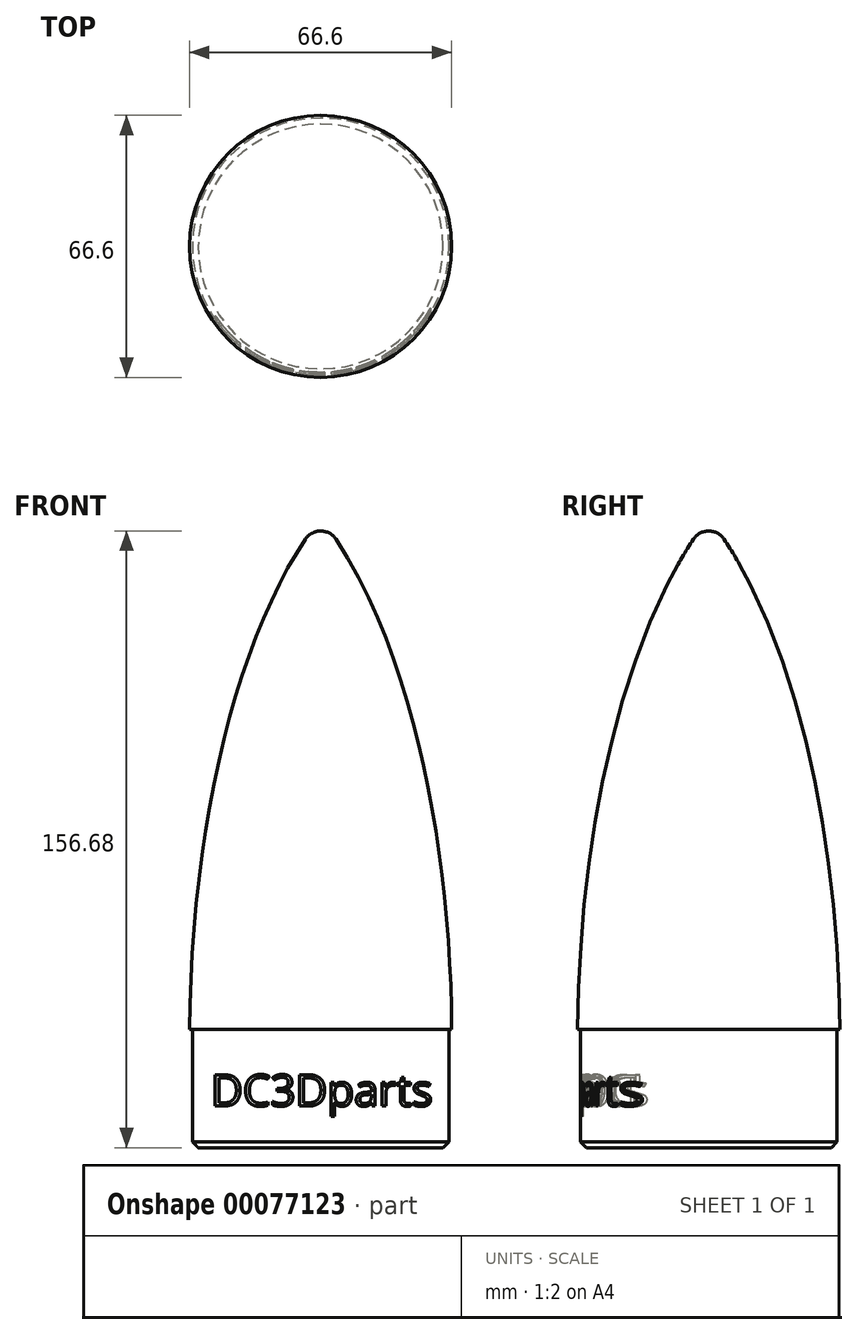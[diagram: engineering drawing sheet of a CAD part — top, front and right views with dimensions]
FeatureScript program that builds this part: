
annotation { "Feature Type Name" : "Feature", "Feature Type Description" : "" }
export const myFeature = defineFeature(function(context is Context, id is Id, definition is map)
    precondition{}
    {
        {
            var Q0;
            Q0=qCreatedBy(makeId("Front.planeOp"),FACE);
            var sketch = newSketch(context, id + "F0", { "sketchPlane" : qUnion([Q0])});
            skEllipticalArc(sketch, "E0", {});
            skLineSegment(sketch, "E1", {"start": v(-33.3, -68.75) * mm, "end": v(-32.6, -68.75) * mm});
            skLineSegment(sketch, "E2", {"start": v(0, -68.75) * mm, "end": v(0, 86.96) * mm});
            skLineSegment(sketch, "E3", {"start": v(0, -68.75) * mm, "end": v(0, -98.75) * mm});
            skLineSegment(sketch, "E4", {"start": v(0, -98.75) * mm, "end": v(-32.6, -98.75) * mm});
            skLineSegment(sketch, "E5", {"start": v(-32.6, -98.75) * mm, "end": v(-32.6, -68.75) * mm});
            skLineSegment(sketch, "E6.trimOffspring", {"start": v(-32.6, -68.75) * mm, "end": v(-33.3, -68.75) * mm});
            skArc(sketch, "E7", {"start": v(0, 57.93) * mm, "mid": v(-2.21, 57.37) * mm, "end": v(-3.9, 55.83) * mm});
            skPoint(sketch, "E8.orphan", {"position": v(0, 61.25) * mm});
            const initialGuessF0  = {"E0": [0.026576005768498712, -0.06619656694530998, 0.016311071592733244, 0.9998669656226756, 0.14465189666781272, 0.059844210815227915, 0.5734099772208412, 1.5951998253377808]};
            skSetInitialGuess(sketch, initialGuessF0);
            skSolve(sketch);
        }
        {
            var Q0;
            Q0=makeQuery(id+"F0.imprint","IMPRINT",FACE,{"disambiguationData":[TD([[makeQuery(id+"F0.imprint","IMPRINT",EDGE,{"derivedFrom":sQuery(id+"F0.wireOp",EDGE,"E0")}),1.0]])]});
            var Q1;
            Q1=sQuery(id+"F0.wireOp",EDGE,"E2");
            revolve(context, id + "F1", {"entities" : qUnion([Q0]), "axis" : qUnion([Q1]), "revolveType" : RevolveType.FULL});
        }
        {
            var Q0;
            Q0=makeQuery(id+"F1.opRevolve","SWEPT_EDGE",EDGE,{"disambiguationData":[OSD([sQuery(id+"F0.wireOp",EDGE,"E4"),sQuery(id+"F0.wireOp",EDGE,"E5")])]});
            chamfer(context, id + "F2", {"entities" : qUnion([Q0]), "width" : 1.5 * mm, "tangentPropagation" : true});
        }
        {
            var Q0;
            Q0=qCreatedBy(makeId("Front.planeOp"),FACE);
            cPlane(context, id + "F3", {"entities" : qUnion([Q0]), "cplaneType" : CPlaneType.OFFSET, "offset" : 40 * mm, "width" : 150 * mm, "height" : 150 * mm});
        }
        {
            var Q0;
            Q0=qCreatedBy(id+"F3.planeOp",FACE);
            var sketch = newSketch(context, id + "F4", { "sketchPlane" : qUnion([Q0])});
            skText(sketch, "E9", { "text": "DC3Dparts", "fontName": "OpenSans-Regular.ttf"});
            const initialGuessF4  = {"E9": [-0.02787, -0.08817, 1, 0, 0.008]};
            skSetInitialGuess(sketch, initialGuessF4);
            skSolve(sketch);
        }
        {
            var Q0;
            Q0 = qSketchRegion(id + "F4", true);
            var Q1;
            Q1=qCreatedBy(makeId("Front.planeOp"),FACE);
            extrude(context, id + "F5", {"entities" : qUnion([Q0]), "endBound" : BoundingType.UP_TO_SURFACE, "oppositeDirection" : true, "depth" : 25 * mm, "endBoundEntityFace" : qUnion([Q1]), "offsetDistance" : 25 * mm});
        }
        {
            var Q0;
            Q0=qCreatedBy(makeId("Front.planeOp"),FACE);
            var sketch = newSketch(context, id + "F6", { "sketchPlane" : qUnion([Q0])});
            skLineSegment(sketch, "E10.bottom", {"start": v(0, -71.45) * mm, "end": v(-32, -71.45) * mm});
            skLineSegment(sketch, "E10.top", {"start": v(0, -104.07) * mm, "end": v(-32, -104.07) * mm});
            skLineSegment(sketch, "E10.left", {"start": v(0, -71.45) * mm, "end": v(0, -104.07) * mm});
            skLineSegment(sketch, "E10.right", {"start": v(-32, -71.45) * mm, "end": v(-32, -104.07) * mm});
            skSolve(sketch);
        }
        {
            var Q0;
            Q0=makeQuery(id+"F6.imprint","IMPRINT",FACE,{"disambiguationData":[TD([[makeQuery(id+"F6.imprint","IMPRINT",EDGE,{"derivedFrom":sQuery(id+"F6.wireOp",EDGE,"E10.bottom")}),1.0]])]});
            var Q1;
            Q1=sQuery(id+"F6.wireOp",EDGE,"E10.left");
            revolve(context, id + "F7", {"entities" : qUnion([Q0]), "axis" : qUnion([Q1]), "revolveType" : RevolveType.FULL});
        }
        {
            var Q0;
            Q0=makeQuery(id+"F7.opRevolve","SWEPT_BODY",BODY,{"disambiguationData":[OSD([sQuery(id+"F6.wireOp",EDGE,"E10.bottom"),sQuery(id+"F6.wireOp",EDGE,"E10.top"),sQuery(id+"F6.wireOp",EDGE,"E10.left"),sQuery(id+"F6.wireOp",EDGE,"E10.right")])]});
            var Q1;
            Q1=makeQuery(id+"F5.opExtrude","SWEPT_BODY",BODY,{"disambiguationData":[OSD([sQuery(id+"F4.wireOp",EDGE,"E9.sketch_text.stroke-0"),sQuery(id+"F4.wireOp",EDGE,"E9.sketch_text.stroke-1"),sQuery(id+"F4.wireOp",EDGE,"E9.sketch_text.stroke-2"),sQuery(id+"F4.wireOp",EDGE,"E9.sketch_text.stroke-3"),sQuery(id+"F4.wireOp",EDGE,"E9.sketch_text.stroke-4"),sQuery(id+"F4.wireOp",EDGE,"E9.sketch_text.stroke-5"),sQuery(id+"F4.wireOp",EDGE,"E9.sketch_text.stroke-6"),sQuery(id+"F4.wireOp",EDGE,"E9.sketch_text.stroke-7"),sQuery(id+"F4.wireOp",EDGE,"E9.sketch_text.stroke-8"),sQuery(id+"F4.wireOp",EDGE,"E9.sketch_text.stroke-9"),sQuery(id+"F4.wireOp",EDGE,"E9.sketch_text.stroke-10"),sQuery(id+"F4.wireOp",EDGE,"E9.sketch_text.stroke-11"),sQuery(id+"F4.wireOp",EDGE,"E9.sketch_text.stroke-12"),sQuery(id+"F4.wireOp",EDGE,"E9.sketch_text.stroke-13")])]});
            var Q2;
            Q2=makeQuery(id+"F5.opExtrude","SWEPT_BODY",BODY,{"disambiguationData":[OSD([sQuery(id+"F4.wireOp",EDGE,"E9.sketch_text.stroke-14"),sQuery(id+"F4.wireOp",EDGE,"E9.sketch_text.stroke-15"),sQuery(id+"F4.wireOp",EDGE,"E9.sketch_text.stroke-16"),sQuery(id+"F4.wireOp",EDGE,"E9.sketch_text.stroke-17"),sQuery(id+"F4.wireOp",EDGE,"E9.sketch_text.stroke-18"),sQuery(id+"F4.wireOp",EDGE,"E9.sketch_text.stroke-19"),sQuery(id+"F4.wireOp",EDGE,"E9.sketch_text.stroke-20"),sQuery(id+"F4.wireOp",EDGE,"E9.sketch_text.stroke-21"),sQuery(id+"F4.wireOp",EDGE,"E9.sketch_text.stroke-22"),sQuery(id+"F4.wireOp",EDGE,"E9.sketch_text.stroke-23"),sQuery(id+"F4.wireOp",EDGE,"E9.sketch_text.stroke-24"),sQuery(id+"F4.wireOp",EDGE,"E9.sketch_text.stroke-25"),sQuery(id+"F4.wireOp",EDGE,"E9.sketch_text.stroke-26"),sQuery(id+"F4.wireOp",EDGE,"E9.sketch_text.stroke-27"),sQuery(id+"F4.wireOp",EDGE,"E9.sketch_text.stroke-28")])]});
            var Q3;
            Q3=makeQuery(id+"F5.opExtrude","SWEPT_BODY",BODY,{"disambiguationData":[OSD([sQuery(id+"F4.wireOp",EDGE,"E9.sketch_text.stroke-29"),sQuery(id+"F4.wireOp",EDGE,"E9.sketch_text.stroke-30"),sQuery(id+"F4.wireOp",EDGE,"E9.sketch_text.stroke-31"),sQuery(id+"F4.wireOp",EDGE,"E9.sketch_text.stroke-32"),sQuery(id+"F4.wireOp",EDGE,"E9.sketch_text.stroke-33"),sQuery(id+"F4.wireOp",EDGE,"E9.sketch_text.stroke-34"),sQuery(id+"F4.wireOp",EDGE,"E9.sketch_text.stroke-35"),sQuery(id+"F4.wireOp",EDGE,"E9.sketch_text.stroke-36"),sQuery(id+"F4.wireOp",EDGE,"E9.sketch_text.stroke-37"),sQuery(id+"F4.wireOp",EDGE,"E9.sketch_text.stroke-38"),sQuery(id+"F4.wireOp",EDGE,"E9.sketch_text.stroke-39"),sQuery(id+"F4.wireOp",EDGE,"E9.sketch_text.stroke-40"),sQuery(id+"F4.wireOp",EDGE,"E9.sketch_text.stroke-41"),sQuery(id+"F4.wireOp",EDGE,"E9.sketch_text.stroke-42"),sQuery(id+"F4.wireOp",EDGE,"E9.sketch_text.stroke-43"),sQuery(id+"F4.wireOp",EDGE,"E9.sketch_text.stroke-44"),sQuery(id+"F4.wireOp",EDGE,"E9.sketch_text.stroke-45"),sQuery(id+"F4.wireOp",EDGE,"E9.sketch_text.stroke-46"),sQuery(id+"F4.wireOp",EDGE,"E9.sketch_text.stroke-47"),sQuery(id+"F4.wireOp",EDGE,"E9.sketch_text.stroke-48"),sQuery(id+"F4.wireOp",EDGE,"E9.sketch_text.stroke-49"),sQuery(id+"F4.wireOp",EDGE,"E9.sketch_text.stroke-50"),sQuery(id+"F4.wireOp",EDGE,"E9.sketch_text.stroke-51"),sQuery(id+"F4.wireOp",EDGE,"E9.sketch_text.stroke-52"),sQuery(id+"F4.wireOp",EDGE,"E9.sketch_text.stroke-53"),sQuery(id+"F4.wireOp",EDGE,"E9.sketch_text.stroke-54"),sQuery(id+"F4.wireOp",EDGE,"E9.sketch_text.stroke-55"),sQuery(id+"F4.wireOp",EDGE,"E9.sketch_text.stroke-56")])]});
            var Q4;
            Q4=makeQuery(id+"F5.opExtrude","SWEPT_BODY",BODY,{"disambiguationData":[OSD([sQuery(id+"F4.wireOp",EDGE,"E9.sketch_text.stroke-57"),sQuery(id+"F4.wireOp",EDGE,"E9.sketch_text.stroke-58"),sQuery(id+"F4.wireOp",EDGE,"E9.sketch_text.stroke-59"),sQuery(id+"F4.wireOp",EDGE,"E9.sketch_text.stroke-60"),sQuery(id+"F4.wireOp",EDGE,"E9.sketch_text.stroke-61"),sQuery(id+"F4.wireOp",EDGE,"E9.sketch_text.stroke-62"),sQuery(id+"F4.wireOp",EDGE,"E9.sketch_text.stroke-63"),sQuery(id+"F4.wireOp",EDGE,"E9.sketch_text.stroke-64"),sQuery(id+"F4.wireOp",EDGE,"E9.sketch_text.stroke-65"),sQuery(id+"F4.wireOp",EDGE,"E9.sketch_text.stroke-66"),sQuery(id+"F4.wireOp",EDGE,"E9.sketch_text.stroke-67"),sQuery(id+"F4.wireOp",EDGE,"E9.sketch_text.stroke-68"),sQuery(id+"F4.wireOp",EDGE,"E9.sketch_text.stroke-69"),sQuery(id+"F4.wireOp",EDGE,"E9.sketch_text.stroke-70")])]});
            var Q5;
            Q5=makeQuery(id+"F5.opExtrude","SWEPT_BODY",BODY,{"disambiguationData":[OSD([sQuery(id+"F4.wireOp",EDGE,"E9.sketch_text.stroke-71"),sQuery(id+"F4.wireOp",EDGE,"E9.sketch_text.stroke-72"),sQuery(id+"F4.wireOp",EDGE,"E9.sketch_text.stroke-73"),sQuery(id+"F4.wireOp",EDGE,"E9.sketch_text.stroke-74"),sQuery(id+"F4.wireOp",EDGE,"E9.sketch_text.stroke-75"),sQuery(id+"F4.wireOp",EDGE,"E9.sketch_text.stroke-76"),sQuery(id+"F4.wireOp",EDGE,"E9.sketch_text.stroke-77"),sQuery(id+"F4.wireOp",EDGE,"E9.sketch_text.stroke-78"),sQuery(id+"F4.wireOp",EDGE,"E9.sketch_text.stroke-79"),sQuery(id+"F4.wireOp",EDGE,"E9.sketch_text.stroke-80"),sQuery(id+"F4.wireOp",EDGE,"E9.sketch_text.stroke-81"),sQuery(id+"F4.wireOp",EDGE,"E9.sketch_text.stroke-82"),sQuery(id+"F4.wireOp",EDGE,"E9.sketch_text.stroke-83"),sQuery(id+"F4.wireOp",EDGE,"E9.sketch_text.stroke-84"),sQuery(id+"F4.wireOp",EDGE,"E9.sketch_text.stroke-85"),sQuery(id+"F4.wireOp",EDGE,"E9.sketch_text.stroke-86"),sQuery(id+"F4.wireOp",EDGE,"E9.sketch_text.stroke-87"),sQuery(id+"F4.wireOp",EDGE,"E9.sketch_text.stroke-88"),sQuery(id+"F4.wireOp",EDGE,"E9.sketch_text.stroke-89"),sQuery(id+"F4.wireOp",EDGE,"E9.sketch_text.stroke-90"),sQuery(id+"F4.wireOp",EDGE,"E9.sketch_text.stroke-91"),sQuery(id+"F4.wireOp",EDGE,"E9.sketch_text.stroke-92"),sQuery(id+"F4.wireOp",EDGE,"E9.sketch_text.stroke-93"),sQuery(id+"F4.wireOp",EDGE,"E9.sketch_text.stroke-94"),sQuery(id+"F4.wireOp",EDGE,"E9.sketch_text.stroke-95")])]});
            var Q6;
            Q6=makeQuery(id+"F5.opExtrude","SWEPT_BODY",BODY,{"disambiguationData":[OSD([sQuery(id+"F4.wireOp",EDGE,"E9.sketch_text.stroke-136"),sQuery(id+"F4.wireOp",EDGE,"E9.sketch_text.stroke-137"),sQuery(id+"F4.wireOp",EDGE,"E9.sketch_text.stroke-138"),sQuery(id+"F4.wireOp",EDGE,"E9.sketch_text.stroke-139"),sQuery(id+"F4.wireOp",EDGE,"E9.sketch_text.stroke-140"),sQuery(id+"F4.wireOp",EDGE,"E9.sketch_text.stroke-141"),sQuery(id+"F4.wireOp",EDGE,"E9.sketch_text.stroke-142"),sQuery(id+"F4.wireOp",EDGE,"E9.sketch_text.stroke-143"),sQuery(id+"F4.wireOp",EDGE,"E9.sketch_text.stroke-144"),sQuery(id+"F4.wireOp",EDGE,"E9.sketch_text.stroke-145"),sQuery(id+"F4.wireOp",EDGE,"E9.sketch_text.stroke-146"),sQuery(id+"F4.wireOp",EDGE,"E9.sketch_text.stroke-147"),sQuery(id+"F4.wireOp",EDGE,"E9.sketch_text.stroke-148"),sQuery(id+"F4.wireOp",EDGE,"E9.sketch_text.stroke-149"),sQuery(id+"F4.wireOp",EDGE,"E9.sketch_text.stroke-150"),sQuery(id+"F4.wireOp",EDGE,"E9.sketch_text.stroke-151"),sQuery(id+"F4.wireOp",EDGE,"E9.sketch_text.stroke-152"),sQuery(id+"F4.wireOp",EDGE,"E9.sketch_text.stroke-153"),sQuery(id+"F4.wireOp",EDGE,"E9.sketch_text.stroke-154")])]});
            var Q7;
            Q7=makeQuery(id+"F5.opExtrude","SWEPT_BODY",BODY,{"disambiguationData":[OSD([sQuery(id+"F4.wireOp",EDGE,"E9.sketch_text.stroke-155"),sQuery(id+"F4.wireOp",EDGE,"E9.sketch_text.stroke-156"),sQuery(id+"F4.wireOp",EDGE,"E9.sketch_text.stroke-157"),sQuery(id+"F4.wireOp",EDGE,"E9.sketch_text.stroke-158"),sQuery(id+"F4.wireOp",EDGE,"E9.sketch_text.stroke-159"),sQuery(id+"F4.wireOp",EDGE,"E9.sketch_text.stroke-160"),sQuery(id+"F4.wireOp",EDGE,"E9.sketch_text.stroke-161"),sQuery(id+"F4.wireOp",EDGE,"E9.sketch_text.stroke-162"),sQuery(id+"F4.wireOp",EDGE,"E9.sketch_text.stroke-163"),sQuery(id+"F4.wireOp",EDGE,"E9.sketch_text.stroke-164"),sQuery(id+"F4.wireOp",EDGE,"E9.sketch_text.stroke-165"),sQuery(id+"F4.wireOp",EDGE,"E9.sketch_text.stroke-166"),sQuery(id+"F4.wireOp",EDGE,"E9.sketch_text.stroke-167"),sQuery(id+"F4.wireOp",EDGE,"E9.sketch_text.stroke-168"),sQuery(id+"F4.wireOp",EDGE,"E9.sketch_text.stroke-169"),sQuery(id+"F4.wireOp",EDGE,"E9.sketch_text.stroke-170"),sQuery(id+"F4.wireOp",EDGE,"E9.sketch_text.stroke-171"),sQuery(id+"F4.wireOp",EDGE,"E9.sketch_text.stroke-172"),sQuery(id+"F4.wireOp",EDGE,"E9.sketch_text.stroke-173"),sQuery(id+"F4.wireOp",EDGE,"E9.sketch_text.stroke-174"),sQuery(id+"F4.wireOp",EDGE,"E9.sketch_text.stroke-175"),sQuery(id+"F4.wireOp",EDGE,"E9.sketch_text.stroke-176"),sQuery(id+"F4.wireOp",EDGE,"E9.sketch_text.stroke-177"),sQuery(id+"F4.wireOp",EDGE,"E9.sketch_text.stroke-178"),sQuery(id+"F4.wireOp",EDGE,"E9.sketch_text.stroke-179")])]});
            var Q8;
            Q8=makeQuery(id+"F5.opExtrude","SWEPT_BODY",BODY,{"disambiguationData":[OSD([sQuery(id+"F4.wireOp",EDGE,"E9.sketch_text.stroke-96"),sQuery(id+"F4.wireOp",EDGE,"E9.sketch_text.stroke-97"),sQuery(id+"F4.wireOp",EDGE,"E9.sketch_text.stroke-98"),sQuery(id+"F4.wireOp",EDGE,"E9.sketch_text.stroke-99"),sQuery(id+"F4.wireOp",EDGE,"E9.sketch_text.stroke-100"),sQuery(id+"F4.wireOp",EDGE,"E9.sketch_text.stroke-101"),sQuery(id+"F4.wireOp",EDGE,"E9.sketch_text.stroke-102"),sQuery(id+"F4.wireOp",EDGE,"E9.sketch_text.stroke-103"),sQuery(id+"F4.wireOp",EDGE,"E9.sketch_text.stroke-104"),sQuery(id+"F4.wireOp",EDGE,"E9.sketch_text.stroke-105"),sQuery(id+"F4.wireOp",EDGE,"E9.sketch_text.stroke-106"),sQuery(id+"F4.wireOp",EDGE,"E9.sketch_text.stroke-107"),sQuery(id+"F4.wireOp",EDGE,"E9.sketch_text.stroke-108"),sQuery(id+"F4.wireOp",EDGE,"E9.sketch_text.stroke-109"),sQuery(id+"F4.wireOp",EDGE,"E9.sketch_text.stroke-110"),sQuery(id+"F4.wireOp",EDGE,"E9.sketch_text.stroke-111"),sQuery(id+"F4.wireOp",EDGE,"E9.sketch_text.stroke-112"),sQuery(id+"F4.wireOp",EDGE,"E9.sketch_text.stroke-113"),sQuery(id+"F4.wireOp",EDGE,"E9.sketch_text.stroke-114"),sQuery(id+"F4.wireOp",EDGE,"E9.sketch_text.stroke-115"),sQuery(id+"F4.wireOp",EDGE,"E9.sketch_text.stroke-116"),sQuery(id+"F4.wireOp",EDGE,"E9.sketch_text.stroke-117"),sQuery(id+"F4.wireOp",EDGE,"E9.sketch_text.stroke-118"),sQuery(id+"F4.wireOp",EDGE,"E9.sketch_text.stroke-119"),sQuery(id+"F4.wireOp",EDGE,"E9.sketch_text.stroke-120"),sQuery(id+"F4.wireOp",EDGE,"E9.sketch_text.stroke-121"),sQuery(id+"F4.wireOp",EDGE,"E9.sketch_text.stroke-122")])]});
            var Q9;
            Q9=makeQuery(id+"F5.opExtrude","SWEPT_BODY",BODY,{"disambiguationData":[OSD([sQuery(id+"F4.wireOp",EDGE,"E9.sketch_text.stroke-123"),sQuery(id+"F4.wireOp",EDGE,"E9.sketch_text.stroke-124"),sQuery(id+"F4.wireOp",EDGE,"E9.sketch_text.stroke-125"),sQuery(id+"F4.wireOp",EDGE,"E9.sketch_text.stroke-126"),sQuery(id+"F4.wireOp",EDGE,"E9.sketch_text.stroke-127"),sQuery(id+"F4.wireOp",EDGE,"E9.sketch_text.stroke-128"),sQuery(id+"F4.wireOp",EDGE,"E9.sketch_text.stroke-129"),sQuery(id+"F4.wireOp",EDGE,"E9.sketch_text.stroke-130"),sQuery(id+"F4.wireOp",EDGE,"E9.sketch_text.stroke-131"),sQuery(id+"F4.wireOp",EDGE,"E9.sketch_text.stroke-132"),sQuery(id+"F4.wireOp",EDGE,"E9.sketch_text.stroke-133"),sQuery(id+"F4.wireOp",EDGE,"E9.sketch_text.stroke-134"),sQuery(id+"F4.wireOp",EDGE,"E9.sketch_text.stroke-135")])]});
            booleanBodies(context, id + "F8", {"operationType" : BooleanOperationType.SUBTRACTION, "tools" : qUnion([Q0]), "targets" : qUnion([Q1, Q2, Q3, Q4, Q5, Q6, Q7, Q8, Q9])});
        }
        {
            var Q0;
            Q0=makeQuery(id+"F5.opExtrude","SWEPT_BODY",BODY,{"disambiguationData":[OSD([sQuery(id+"F4.wireOp",EDGE,"E9.sketch_text.stroke-0"),sQuery(id+"F4.wireOp",EDGE,"E9.sketch_text.stroke-1"),sQuery(id+"F4.wireOp",EDGE,"E9.sketch_text.stroke-2"),sQuery(id+"F4.wireOp",EDGE,"E9.sketch_text.stroke-3"),sQuery(id+"F4.wireOp",EDGE,"E9.sketch_text.stroke-4"),sQuery(id+"F4.wireOp",EDGE,"E9.sketch_text.stroke-5"),sQuery(id+"F4.wireOp",EDGE,"E9.sketch_text.stroke-6"),sQuery(id+"F4.wireOp",EDGE,"E9.sketch_text.stroke-7"),sQuery(id+"F4.wireOp",EDGE,"E9.sketch_text.stroke-8"),sQuery(id+"F4.wireOp",EDGE,"E9.sketch_text.stroke-9"),sQuery(id+"F4.wireOp",EDGE,"E9.sketch_text.stroke-10"),sQuery(id+"F4.wireOp",EDGE,"E9.sketch_text.stroke-11"),sQuery(id+"F4.wireOp",EDGE,"E9.sketch_text.stroke-12"),sQuery(id+"F4.wireOp",EDGE,"E9.sketch_text.stroke-13")])]});
            var Q1;
            Q1=makeQuery(id+"F5.opExtrude","SWEPT_BODY",BODY,{"disambiguationData":[OSD([sQuery(id+"F4.wireOp",EDGE,"E9.sketch_text.stroke-14"),sQuery(id+"F4.wireOp",EDGE,"E9.sketch_text.stroke-15"),sQuery(id+"F4.wireOp",EDGE,"E9.sketch_text.stroke-16"),sQuery(id+"F4.wireOp",EDGE,"E9.sketch_text.stroke-17"),sQuery(id+"F4.wireOp",EDGE,"E9.sketch_text.stroke-18"),sQuery(id+"F4.wireOp",EDGE,"E9.sketch_text.stroke-19"),sQuery(id+"F4.wireOp",EDGE,"E9.sketch_text.stroke-20"),sQuery(id+"F4.wireOp",EDGE,"E9.sketch_text.stroke-21"),sQuery(id+"F4.wireOp",EDGE,"E9.sketch_text.stroke-22"),sQuery(id+"F4.wireOp",EDGE,"E9.sketch_text.stroke-23"),sQuery(id+"F4.wireOp",EDGE,"E9.sketch_text.stroke-24"),sQuery(id+"F4.wireOp",EDGE,"E9.sketch_text.stroke-25"),sQuery(id+"F4.wireOp",EDGE,"E9.sketch_text.stroke-26"),sQuery(id+"F4.wireOp",EDGE,"E9.sketch_text.stroke-27"),sQuery(id+"F4.wireOp",EDGE,"E9.sketch_text.stroke-28")])]});
            var Q2;
            Q2=makeQuery(id+"F5.opExtrude","SWEPT_BODY",BODY,{"disambiguationData":[OSD([sQuery(id+"F4.wireOp",EDGE,"E9.sketch_text.stroke-29"),sQuery(id+"F4.wireOp",EDGE,"E9.sketch_text.stroke-30"),sQuery(id+"F4.wireOp",EDGE,"E9.sketch_text.stroke-31"),sQuery(id+"F4.wireOp",EDGE,"E9.sketch_text.stroke-32"),sQuery(id+"F4.wireOp",EDGE,"E9.sketch_text.stroke-33"),sQuery(id+"F4.wireOp",EDGE,"E9.sketch_text.stroke-34"),sQuery(id+"F4.wireOp",EDGE,"E9.sketch_text.stroke-35"),sQuery(id+"F4.wireOp",EDGE,"E9.sketch_text.stroke-36"),sQuery(id+"F4.wireOp",EDGE,"E9.sketch_text.stroke-37"),sQuery(id+"F4.wireOp",EDGE,"E9.sketch_text.stroke-38"),sQuery(id+"F4.wireOp",EDGE,"E9.sketch_text.stroke-39"),sQuery(id+"F4.wireOp",EDGE,"E9.sketch_text.stroke-40"),sQuery(id+"F4.wireOp",EDGE,"E9.sketch_text.stroke-41"),sQuery(id+"F4.wireOp",EDGE,"E9.sketch_text.stroke-42"),sQuery(id+"F4.wireOp",EDGE,"E9.sketch_text.stroke-43"),sQuery(id+"F4.wireOp",EDGE,"E9.sketch_text.stroke-44"),sQuery(id+"F4.wireOp",EDGE,"E9.sketch_text.stroke-45"),sQuery(id+"F4.wireOp",EDGE,"E9.sketch_text.stroke-46"),sQuery(id+"F4.wireOp",EDGE,"E9.sketch_text.stroke-47"),sQuery(id+"F4.wireOp",EDGE,"E9.sketch_text.stroke-48"),sQuery(id+"F4.wireOp",EDGE,"E9.sketch_text.stroke-49"),sQuery(id+"F4.wireOp",EDGE,"E9.sketch_text.stroke-50"),sQuery(id+"F4.wireOp",EDGE,"E9.sketch_text.stroke-51"),sQuery(id+"F4.wireOp",EDGE,"E9.sketch_text.stroke-52"),sQuery(id+"F4.wireOp",EDGE,"E9.sketch_text.stroke-53"),sQuery(id+"F4.wireOp",EDGE,"E9.sketch_text.stroke-54"),sQuery(id+"F4.wireOp",EDGE,"E9.sketch_text.stroke-55"),sQuery(id+"F4.wireOp",EDGE,"E9.sketch_text.stroke-56")])]});
            var Q3;
            Q3=makeQuery(id+"F5.opExtrude","SWEPT_BODY",BODY,{"disambiguationData":[OSD([sQuery(id+"F4.wireOp",EDGE,"E9.sketch_text.stroke-57"),sQuery(id+"F4.wireOp",EDGE,"E9.sketch_text.stroke-58"),sQuery(id+"F4.wireOp",EDGE,"E9.sketch_text.stroke-59"),sQuery(id+"F4.wireOp",EDGE,"E9.sketch_text.stroke-60"),sQuery(id+"F4.wireOp",EDGE,"E9.sketch_text.stroke-61"),sQuery(id+"F4.wireOp",EDGE,"E9.sketch_text.stroke-62"),sQuery(id+"F4.wireOp",EDGE,"E9.sketch_text.stroke-63"),sQuery(id+"F4.wireOp",EDGE,"E9.sketch_text.stroke-64"),sQuery(id+"F4.wireOp",EDGE,"E9.sketch_text.stroke-65"),sQuery(id+"F4.wireOp",EDGE,"E9.sketch_text.stroke-66"),sQuery(id+"F4.wireOp",EDGE,"E9.sketch_text.stroke-67"),sQuery(id+"F4.wireOp",EDGE,"E9.sketch_text.stroke-68"),sQuery(id+"F4.wireOp",EDGE,"E9.sketch_text.stroke-69"),sQuery(id+"F4.wireOp",EDGE,"E9.sketch_text.stroke-70")])]});
            var Q4;
            Q4=makeQuery(id+"F5.opExtrude","SWEPT_BODY",BODY,{"disambiguationData":[OSD([sQuery(id+"F4.wireOp",EDGE,"E9.sketch_text.stroke-71"),sQuery(id+"F4.wireOp",EDGE,"E9.sketch_text.stroke-72"),sQuery(id+"F4.wireOp",EDGE,"E9.sketch_text.stroke-73"),sQuery(id+"F4.wireOp",EDGE,"E9.sketch_text.stroke-74"),sQuery(id+"F4.wireOp",EDGE,"E9.sketch_text.stroke-75"),sQuery(id+"F4.wireOp",EDGE,"E9.sketch_text.stroke-76"),sQuery(id+"F4.wireOp",EDGE,"E9.sketch_text.stroke-77"),sQuery(id+"F4.wireOp",EDGE,"E9.sketch_text.stroke-78"),sQuery(id+"F4.wireOp",EDGE,"E9.sketch_text.stroke-79"),sQuery(id+"F4.wireOp",EDGE,"E9.sketch_text.stroke-80"),sQuery(id+"F4.wireOp",EDGE,"E9.sketch_text.stroke-81"),sQuery(id+"F4.wireOp",EDGE,"E9.sketch_text.stroke-82"),sQuery(id+"F4.wireOp",EDGE,"E9.sketch_text.stroke-83"),sQuery(id+"F4.wireOp",EDGE,"E9.sketch_text.stroke-84"),sQuery(id+"F4.wireOp",EDGE,"E9.sketch_text.stroke-85"),sQuery(id+"F4.wireOp",EDGE,"E9.sketch_text.stroke-86"),sQuery(id+"F4.wireOp",EDGE,"E9.sketch_text.stroke-87"),sQuery(id+"F4.wireOp",EDGE,"E9.sketch_text.stroke-88"),sQuery(id+"F4.wireOp",EDGE,"E9.sketch_text.stroke-89"),sQuery(id+"F4.wireOp",EDGE,"E9.sketch_text.stroke-90"),sQuery(id+"F4.wireOp",EDGE,"E9.sketch_text.stroke-91"),sQuery(id+"F4.wireOp",EDGE,"E9.sketch_text.stroke-92"),sQuery(id+"F4.wireOp",EDGE,"E9.sketch_text.stroke-93"),sQuery(id+"F4.wireOp",EDGE,"E9.sketch_text.stroke-94"),sQuery(id+"F4.wireOp",EDGE,"E9.sketch_text.stroke-95")])]});
            var Q5;
            Q5=makeQuery(id+"F5.opExtrude","SWEPT_BODY",BODY,{"disambiguationData":[OSD([sQuery(id+"F4.wireOp",EDGE,"E9.sketch_text.stroke-96"),sQuery(id+"F4.wireOp",EDGE,"E9.sketch_text.stroke-97"),sQuery(id+"F4.wireOp",EDGE,"E9.sketch_text.stroke-98"),sQuery(id+"F4.wireOp",EDGE,"E9.sketch_text.stroke-99"),sQuery(id+"F4.wireOp",EDGE,"E9.sketch_text.stroke-100"),sQuery(id+"F4.wireOp",EDGE,"E9.sketch_text.stroke-101"),sQuery(id+"F4.wireOp",EDGE,"E9.sketch_text.stroke-102"),sQuery(id+"F4.wireOp",EDGE,"E9.sketch_text.stroke-103"),sQuery(id+"F4.wireOp",EDGE,"E9.sketch_text.stroke-104"),sQuery(id+"F4.wireOp",EDGE,"E9.sketch_text.stroke-105"),sQuery(id+"F4.wireOp",EDGE,"E9.sketch_text.stroke-106"),sQuery(id+"F4.wireOp",EDGE,"E9.sketch_text.stroke-107"),sQuery(id+"F4.wireOp",EDGE,"E9.sketch_text.stroke-108"),sQuery(id+"F4.wireOp",EDGE,"E9.sketch_text.stroke-109"),sQuery(id+"F4.wireOp",EDGE,"E9.sketch_text.stroke-110"),sQuery(id+"F4.wireOp",EDGE,"E9.sketch_text.stroke-111"),sQuery(id+"F4.wireOp",EDGE,"E9.sketch_text.stroke-112"),sQuery(id+"F4.wireOp",EDGE,"E9.sketch_text.stroke-113"),sQuery(id+"F4.wireOp",EDGE,"E9.sketch_text.stroke-114"),sQuery(id+"F4.wireOp",EDGE,"E9.sketch_text.stroke-115"),sQuery(id+"F4.wireOp",EDGE,"E9.sketch_text.stroke-116"),sQuery(id+"F4.wireOp",EDGE,"E9.sketch_text.stroke-117"),sQuery(id+"F4.wireOp",EDGE,"E9.sketch_text.stroke-118"),sQuery(id+"F4.wireOp",EDGE,"E9.sketch_text.stroke-119"),sQuery(id+"F4.wireOp",EDGE,"E9.sketch_text.stroke-120"),sQuery(id+"F4.wireOp",EDGE,"E9.sketch_text.stroke-121"),sQuery(id+"F4.wireOp",EDGE,"E9.sketch_text.stroke-122")])]});
            var Q6;
            Q6=makeQuery(id+"F5.opExtrude","SWEPT_BODY",BODY,{"disambiguationData":[OSD([sQuery(id+"F4.wireOp",EDGE,"E9.sketch_text.stroke-123"),sQuery(id+"F4.wireOp",EDGE,"E9.sketch_text.stroke-124"),sQuery(id+"F4.wireOp",EDGE,"E9.sketch_text.stroke-125"),sQuery(id+"F4.wireOp",EDGE,"E9.sketch_text.stroke-126"),sQuery(id+"F4.wireOp",EDGE,"E9.sketch_text.stroke-127"),sQuery(id+"F4.wireOp",EDGE,"E9.sketch_text.stroke-128"),sQuery(id+"F4.wireOp",EDGE,"E9.sketch_text.stroke-129"),sQuery(id+"F4.wireOp",EDGE,"E9.sketch_text.stroke-130"),sQuery(id+"F4.wireOp",EDGE,"E9.sketch_text.stroke-131"),sQuery(id+"F4.wireOp",EDGE,"E9.sketch_text.stroke-132"),sQuery(id+"F4.wireOp",EDGE,"E9.sketch_text.stroke-133"),sQuery(id+"F4.wireOp",EDGE,"E9.sketch_text.stroke-134"),sQuery(id+"F4.wireOp",EDGE,"E9.sketch_text.stroke-135")])]});
            var Q7;
            Q7=makeQuery(id+"F5.opExtrude","SWEPT_BODY",BODY,{"disambiguationData":[OSD([sQuery(id+"F4.wireOp",EDGE,"E9.sketch_text.stroke-155"),sQuery(id+"F4.wireOp",EDGE,"E9.sketch_text.stroke-156"),sQuery(id+"F4.wireOp",EDGE,"E9.sketch_text.stroke-157"),sQuery(id+"F4.wireOp",EDGE,"E9.sketch_text.stroke-158"),sQuery(id+"F4.wireOp",EDGE,"E9.sketch_text.stroke-159"),sQuery(id+"F4.wireOp",EDGE,"E9.sketch_text.stroke-160"),sQuery(id+"F4.wireOp",EDGE,"E9.sketch_text.stroke-161"),sQuery(id+"F4.wireOp",EDGE,"E9.sketch_text.stroke-162"),sQuery(id+"F4.wireOp",EDGE,"E9.sketch_text.stroke-163"),sQuery(id+"F4.wireOp",EDGE,"E9.sketch_text.stroke-164"),sQuery(id+"F4.wireOp",EDGE,"E9.sketch_text.stroke-165"),sQuery(id+"F4.wireOp",EDGE,"E9.sketch_text.stroke-166"),sQuery(id+"F4.wireOp",EDGE,"E9.sketch_text.stroke-167"),sQuery(id+"F4.wireOp",EDGE,"E9.sketch_text.stroke-168"),sQuery(id+"F4.wireOp",EDGE,"E9.sketch_text.stroke-169"),sQuery(id+"F4.wireOp",EDGE,"E9.sketch_text.stroke-170"),sQuery(id+"F4.wireOp",EDGE,"E9.sketch_text.stroke-171"),sQuery(id+"F4.wireOp",EDGE,"E9.sketch_text.stroke-172"),sQuery(id+"F4.wireOp",EDGE,"E9.sketch_text.stroke-173"),sQuery(id+"F4.wireOp",EDGE,"E9.sketch_text.stroke-174"),sQuery(id+"F4.wireOp",EDGE,"E9.sketch_text.stroke-175"),sQuery(id+"F4.wireOp",EDGE,"E9.sketch_text.stroke-176"),sQuery(id+"F4.wireOp",EDGE,"E9.sketch_text.stroke-177"),sQuery(id+"F4.wireOp",EDGE,"E9.sketch_text.stroke-178"),sQuery(id+"F4.wireOp",EDGE,"E9.sketch_text.stroke-179")])]});
            var Q8;
            Q8=makeQuery(id+"F5.opExtrude","SWEPT_BODY",BODY,{"disambiguationData":[OSD([sQuery(id+"F4.wireOp",EDGE,"E9.sketch_text.stroke-136"),sQuery(id+"F4.wireOp",EDGE,"E9.sketch_text.stroke-137"),sQuery(id+"F4.wireOp",EDGE,"E9.sketch_text.stroke-138"),sQuery(id+"F4.wireOp",EDGE,"E9.sketch_text.stroke-139"),sQuery(id+"F4.wireOp",EDGE,"E9.sketch_text.stroke-140"),sQuery(id+"F4.wireOp",EDGE,"E9.sketch_text.stroke-141"),sQuery(id+"F4.wireOp",EDGE,"E9.sketch_text.stroke-142"),sQuery(id+"F4.wireOp",EDGE,"E9.sketch_text.stroke-143"),sQuery(id+"F4.wireOp",EDGE,"E9.sketch_text.stroke-144"),sQuery(id+"F4.wireOp",EDGE,"E9.sketch_text.stroke-145"),sQuery(id+"F4.wireOp",EDGE,"E9.sketch_text.stroke-146"),sQuery(id+"F4.wireOp",EDGE,"E9.sketch_text.stroke-147"),sQuery(id+"F4.wireOp",EDGE,"E9.sketch_text.stroke-148"),sQuery(id+"F4.wireOp",EDGE,"E9.sketch_text.stroke-149"),sQuery(id+"F4.wireOp",EDGE,"E9.sketch_text.stroke-150"),sQuery(id+"F4.wireOp",EDGE,"E9.sketch_text.stroke-151"),sQuery(id+"F4.wireOp",EDGE,"E9.sketch_text.stroke-152"),sQuery(id+"F4.wireOp",EDGE,"E9.sketch_text.stroke-153"),sQuery(id+"F4.wireOp",EDGE,"E9.sketch_text.stroke-154")])]});
            var Q9;
            Q9=makeQuery(id+"F1.opRevolve","SWEPT_BODY",BODY,{"disambiguationData":[OSD([sQuery(id+"F0.wireOp",EDGE,"E0"),sQuery(id+"F0.wireOp",EDGE,"E2"),sQuery(id+"F0.wireOp",EDGE,"E3"),sQuery(id+"F0.wireOp",EDGE,"E4"),sQuery(id+"F0.wireOp",EDGE,"E5"),sQuery(id+"F0.wireOp",EDGE,"E6.trimOffspring"),sQuery(id+"F0.wireOp",EDGE,"E7")])]});
            booleanBodies(context, id + "F9", {"operationType" : BooleanOperationType.SUBTRACTION, "tools" : qUnion([Q0, Q1, Q2, Q3, Q4, Q5, Q6, Q7, Q8]), "targets" : qUnion([Q9])});
        }
    });
